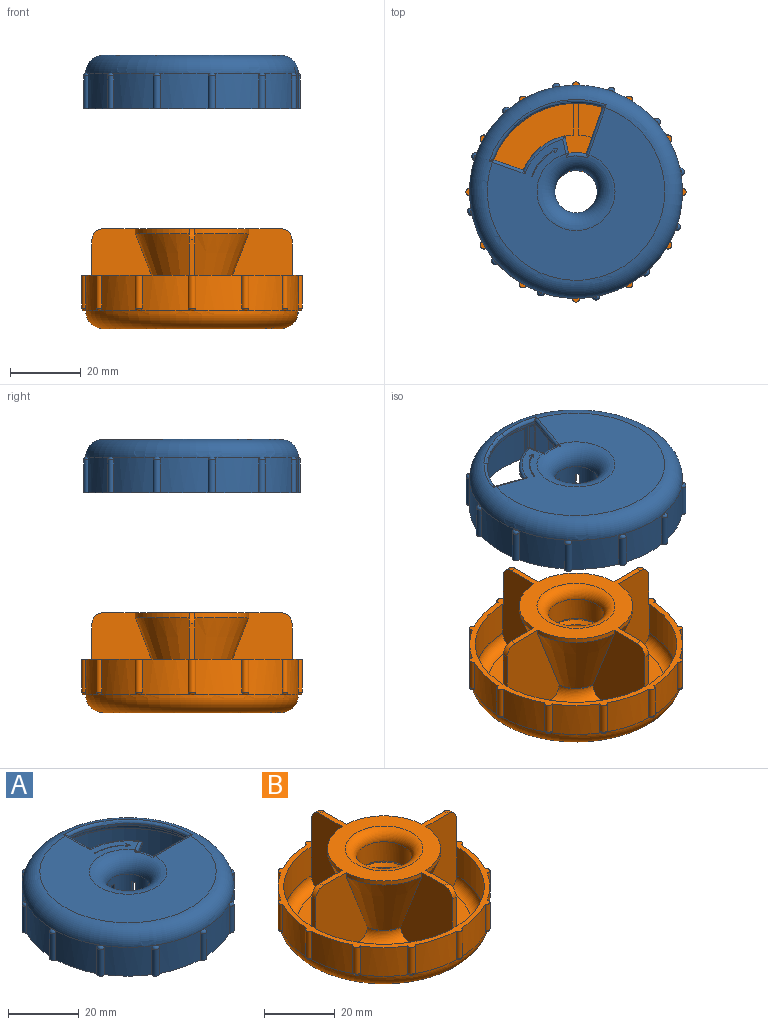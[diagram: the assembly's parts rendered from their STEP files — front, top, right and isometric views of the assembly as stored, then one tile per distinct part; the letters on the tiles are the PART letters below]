
ASSEMBLY  parts=2 mates=1
PART A: 140 faces, bbox 66.1x66.1x16.2 mm
  f0: plane 50x50mm, normal (0,0,1), area 1238.5mm2, adj f77,f103,f117,f119,f120,f123,f127,f128
  f1: cylinder r=7.6mm len=5.77mm, axis (0,0,-1), area 8.6mm2, adj f2,f8,f44,f125
  f2: plane 5.77x4.13mm, normal (0,0,-1), area 9.7mm2, adj f1,f8,f43,f125
  f3: cone r=8.62mm half-angle=41.6deg, axis (0,0,-1), area 6mm2, adj f8,f42,f46,f125
  f4: torus R=7.55mm, axis (0,0,1), area 8.8mm2, adj f5,f7,f11,f16
  f5: cone r=8.62mm half-angle=41.6deg, axis (0,0,1), area 6mm2, adj f4,f7,f9,f16
  f6: plane 1.92x1.73mm, normal (0,0,-1), area 1.7mm2, adj f7,f8,f42,f43
  f7: plane 7.43x2.07mm, normal (0.5,-0.87,0), area 13mm2, adj f4,f5,f6,f9,f10,f11,f42,f43
  f8: plane 7.43x2.07mm, normal (-0.5,0.87,0), area 13mm2, adj f1,f2,f3,f6,f42,f43,f44,f46
  f9: cylinder r=7.6mm len=6.66mm, axis (0,0,-1), area 8.6mm2, adj f5,f7,f10,f16
  f10: plane 6.66x2.16mm, normal (0,0,-1), area 9.7mm2, adj f7,f9,f16,f43
  f11: cone r=8.62mm half-angle=41.6deg, axis (0,0,-1), area 6mm2, adj f4,f7,f16,f42
  f12: torus R=7.55mm, axis (0,0,1), area 8.8mm2, adj f13,f15,f19,f24
  f13: cone r=8.62mm half-angle=41.6deg, axis (0,0,1), area 6mm2, adj f12,f15,f17,f24
  f14: plane 1.92x1.73mm, normal (0,0,-1), area 1.7mm2, adj f15,f16,f42,f43
  f15: plane 7.43x2.07mm, normal (-0.5,-0.87,0), area 13mm2, adj f12,f13,f14,f17,f18,f19,f42,f43
  f16: plane 7.43x2.07mm, normal (0.5,0.87,0), area 13mm2, adj f4,f5,f9,f10,f11,f14,f42,f43
  f17: cylinder r=7.6mm len=5.77mm, axis (0,0,-1), area 8.6mm2, adj f13,f15,f18,f24
  f18: plane 5.77x4.13mm, normal (0,0,-1), area 9.7mm2, adj f15,f17,f24,f43
  f19: cone r=8.62mm half-angle=41.6deg, axis (0,0,-1), area 6mm2, adj f12,f15,f24,f42
  f20: torus R=7.55mm, axis (0,0,1), area 8.8mm2, adj f21,f23,f27,f32
  f21: cone r=8.62mm half-angle=41.6deg, axis (0,0,1), area 6mm2, adj f20,f23,f25,f32
  f22: plane 1.62x1.07mm, normal (0,0,-1), area 1.7mm2, adj f23,f24,f42,f43
  f23: plane 7.43x2.39mm, normal (-1,0,0), area 13mm2, adj f20,f21,f22,f25,f26,f27,f42,f43
  f24: plane 7.43x2.39mm, normal (1,0,0), area 13mm2, adj f12,f13,f17,f18,f19,f22,f42,f43
  f25: cylinder r=7.6mm len=5.77mm, axis (0,0,-1), area 8.6mm2, adj f21,f23,f26,f32
  f26: plane 5.77x4.13mm, normal (0,0,-1), area 9.7mm2, adj f23,f25,f32,f43
  f27: cone r=8.62mm half-angle=41.6deg, axis (0,0,-1), area 6mm2, adj f20,f23,f32,f42
  f28: torus R=7.55mm, axis (0,0,1), area 8.8mm2, adj f29,f31,f35,f40
  f29: cone r=8.62mm half-angle=41.6deg, axis (0,0,1), area 6mm2, adj f28,f31,f33,f40
  f30: plane 1.92x1.73mm, normal (0,0,-1), area 1.7mm2, adj f31,f32,f42,f43
  f31: plane 7.43x2.07mm, normal (-0.5,0.87,0), area 13mm2, adj f28,f29,f30,f33,f34,f35,f42,f43
  f32: plane 7.43x2.07mm, normal (0.5,-0.87,0), area 13mm2, adj f20,f21,f25,f26,f27,f30,f42,f43
  f33: cylinder r=7.6mm len=6.66mm, axis (0,0,-1), area 8.6mm2, adj f29,f31,f34,f40
  f34: plane 6.66x2.16mm, normal (0,0,-1), area 9.7mm2, adj f31,f33,f40,f43
  f35: cone r=8.62mm half-angle=41.6deg, axis (0,0,-1), area 6mm2, adj f28,f31,f40,f42
  f36: torus R=7.55mm, axis (0,0,1), area 8.8mm2, adj f37,f39,f45,f126
  f37: cone r=8.62mm half-angle=41.6deg, axis (0,0,1), area 6mm2, adj f36,f39,f41,f126
  f38: plane 1.92x1.73mm, normal (0,0,-1), area 1.7mm2, adj f39,f40,f42,f43
  f39: plane 7.43x2.07mm, normal (0.5,0.87,0), area 13mm2, adj f36,f37,f38,f41,f42,f43,f45,f53
  f40: plane 7.43x2.07mm, normal (-0.5,-0.87,0), area 13mm2, adj f28,f29,f33,f34,f35,f38,f42,f43
  f41: cylinder r=7.6mm len=5.77mm, axis (0,0,-1), area 8.6mm2, adj f37,f39,f53,f126
  f42: cylinder r=7.6mm len=15.2mm, axis (0,0,-1), area 283.2mm2, adj f3,f6,f7,f8,f11,f14,f15,f16
  f43: cylinder r=6mm len=12mm, axis (0,0,-1), area 329.6mm2, adj f2,f6,f7,f8,f10,f14,f15,f16
  f44: cone r=8.62mm half-angle=41.6deg, axis (0,0,1), area 6mm2, adj f1,f8,f46,f125
  f45: cone r=8.62mm half-angle=41.6deg, axis (0,0,-1), area 6mm2, adj f36,f39,f42,f126
  f46: torus R=7.55mm, axis (0,0,1), area 8.8mm2, adj f3,f8,f44,f125
  f47: cylinder r=28.4mm len=10mm, axis (0,0,-1), area 16.5mm2, adj f51,f52,f104,f106
  f48: cylinder r=28.4mm len=56.8mm, axis (0,0,-1), area 1711mm2, adj f51,f52,f105,f107
  f49: plane 50x50mm, normal (0,0,-1), area 1276.1mm2, adj f50,f51,f109,f110,f111,f112
  f50: torus R=11mm, axis (0,0,1), area 296.5mm2, adj f42,f49,f113
  f51: torus R=25mm, axis (0,0,1), area 906.8mm2, adj f47,f48,f49,f104,f105,f106,f107,f108
  f52: plane 62.13x62.13mm, normal (0,0,-1), area 316.5mm2, adj f47,f48,f79,f80,f81,f82,f83,f84
  f53: plane 5.77x4.13mm, normal (0,0,-1), area 9.7mm2, adj f39,f41,f43,f126
  f54: plane 1.56x1.47mm, normal (0,0,1), area 0.1mm2, adj f76,f77
  f55: plane 1.56x1.47mm, normal (0,0,1), area 0.1mm2, adj f66,f77
  f56: plane 1.6x1.33mm, normal (0,0,1), area 0.1mm2, adj f67,f77
  f57: plane 1.56x1.47mm, normal (0,0,1), area 0.1mm2, adj f68,f77
  f58: plane 1.56x1.47mm, normal (0,0,1), area 0.1mm2, adj f69,f77
  f59: plane 1.6x1.33mm, normal (0,0,1), area 0.1mm2, adj f70,f77
  f60: plane 1.56x1.47mm, normal (0,0,1), area 0.1mm2, adj f71,f77
  f61: plane 1.56x1.47mm, normal (0,0,1), area 0.1mm2, adj f72,f77
  f62: plane 1.6x1.33mm, normal (0,0,1), area 0.1mm2, adj f73,f77
  f63: plane 1.56x1.47mm, normal (0,0,1), area 0.1mm2, adj f74,f77
  f64: plane 1.56x1.47mm, normal (0,0,1), area 0.1mm2, adj f75,f77
  f65: plane 1.6x1.33mm, normal (0,0,1), area 0.1mm2, adj f77,f78
  f66: torus R=0.27mm, axis (0,0,1), area 4.3mm2, adj f55,f79,f100,f102
  f67: torus R=0.27mm, axis (0,0,1), area 4.3mm2, adj f56,f80,f99,f100
  f68: torus R=0.27mm, axis (0,0,1), area 4.3mm2, adj f57,f81,f98,f99
  f69: torus R=0.27mm, axis (0,0,1), area 4.3mm2, adj f58,f82,f97,f98
  f70: torus R=0.27mm, axis (0,0,1), area 4.3mm2, adj f59,f83,f96,f97
  f71: torus R=0.27mm, axis (0,0,1), area 4.3mm2, adj f60,f84,f95,f96
  f72: torus R=0.27mm, axis (0,0,1), area 4.3mm2, adj f61,f85,f94,f95
  f73: torus R=0.27mm, axis (0,0,1), area 4.3mm2, adj f62,f86,f93,f94
  f74: torus R=0.27mm, axis (0,0,1), area 4.3mm2, adj f63,f87,f92,f93
  f75: torus R=0.27mm, axis (0,0,1), area 4.3mm2, adj f64,f88,f91,f92
  f76: torus R=0.27mm, axis (0,0,1), area 4.3mm2, adj f54,f90,f101,f102
  f77: torus R=25mm, axis (0,0,1), area 1352.4mm2, adj f0,f54,f55,f56,f57,f58,f59,f60
  f78: torus R=0.27mm, axis (0,0,1), area 4.3mm2, adj f65,f89,f90,f91
  f79: cylinder r=1.07mm len=9.2mm, axis (0,0,-1), area 31.2mm2, adj f52,f66,f100,f102
  f80: cylinder r=1.07mm len=9.2mm, axis (0,0,-1), area 31.2mm2, adj f52,f67,f99,f100
  f81: cylinder r=1.07mm len=9.2mm, axis (0,0,-1), area 31.2mm2, adj f52,f68,f98,f99
  f82: cylinder r=1.07mm len=9.2mm, axis (0,0,-1), area 31.2mm2, adj f52,f69,f97,f98
  f83: cylinder r=1.07mm len=9.2mm, axis (0,0,-1), area 31.2mm2, adj f52,f70,f96,f97
  f84: cylinder r=1.07mm len=9.2mm, axis (0,0,-1), area 31.2mm2, adj f52,f71,f95,f96
  f85: cylinder r=1.07mm len=9.2mm, axis (0,0,-1), area 31.2mm2, adj f52,f72,f94,f95
  f86: cylinder r=1.07mm len=9.2mm, axis (0,0,-1), area 31.2mm2, adj f52,f73,f93,f94
  f87: cylinder r=1.07mm len=9.2mm, axis (0,0,-1), area 31.2mm2, adj f52,f74,f92,f93
  f88: cylinder r=1.07mm len=9.2mm, axis (0,0,-1), area 31.2mm2, adj f52,f75,f91,f92
  f89: cylinder r=1.07mm len=9.2mm, axis (0,0,-1), area 31.2mm2, adj f52,f78,f90,f91
  f90: cylinder r=30mm len=14.5mm, axis (0,0,-1), area 136.4mm2, adj f52,f76,f77,f78,f89,f101
  f91: cylinder r=30mm len=14.5mm, axis (0,0,-1), area 136.4mm2, adj f52,f75,f77,f78,f88,f89
  f92: cylinder r=30mm len=10.62mm, axis (0,0,-1), area 136.4mm2, adj f52,f74,f75,f77,f87,f88
  f93: cylinder r=30mm len=14.5mm, axis (0,0,-1), area 136.4mm2, adj f52,f73,f74,f77,f86,f87
  f94: cylinder r=30mm len=14.5mm, axis (0,0,-1), area 136.4mm2, adj f52,f72,f73,f77,f85,f86
  f95: cylinder r=30mm len=10.62mm, axis (0,0,-1), area 136.4mm2, adj f52,f71,f72,f77,f84,f85
  f96: cylinder r=30mm len=14.5mm, axis (0,0,-1), area 136.4mm2, adj f52,f70,f71,f77,f83,f84
  f97: cylinder r=30mm len=14.5mm, axis (0,0,-1), area 136.4mm2, adj f52,f69,f70,f77,f82,f83
  f98: cylinder r=30mm len=10.62mm, axis (0,0,-1), area 136.4mm2, adj f52,f68,f69,f77,f81,f82
  f99: cylinder r=30mm len=14.5mm, axis (0,0,-1), area 136.4mm2, adj f52,f67,f68,f77,f80,f81
  f100: cylinder r=30mm len=14.5mm, axis (0,0,-1), area 136.4mm2, adj f52,f66,f67,f77,f79,f80
  f101: cylinder r=1.07mm len=9.2mm, axis (0,0,-1), area 31.2mm2, adj f52,f76,f90,f102
  f102: cylinder r=30mm len=10.62mm, axis (0,0,-1), area 136.4mm2, adj f52,f66,f76,f77,f79,f101
  f103: torus R=11mm, axis (0,0,1), area 379.6mm2, adj f0,f43,f114,f115,f116
  f104: plane 11.61x0.41mm, normal (0,1,0), area 4.4mm2, adj f47,f51,f52,f105
  f105: plane 12.75x5.17mm, normal (-1,0,0), area 45mm2, adj f48,f51,f52,f104
  f106: plane 11.98x1.18mm, normal (-0.88,-0.48,0), area 10.1mm2, adj f47,f51,f52,f107
  f107: plane 11.98x1.22mm, normal (-0.93,0.37,0), area 10.1mm2, adj f48,f51,f52,f106
  f108: cylinder r=25mm len=24.19mm, axis (0,0,-1), area 27.2mm2, adj f51,f109,f111,f122
  f109: plane 9.01x0.8mm, normal (1,0,0), area 7.2mm2, adj f49,f108,f110,f122,f123
  f110: cylinder r=16mm len=12.99mm, axis (0,0,-1), area 12.7mm2, adj f49,f109,f112,f120
  f111: plane 14.02x0.8mm, normal (0,1,0), area 11.2mm2, adj f49,f108,f113,f114,f116,f119,f122
  f112: plane 4.31x2.54mm, normal (0.51,-0.86,0), area 4mm2, adj f49,f110,f113,f114,f117
  f113: cylinder r=11mm len=4.77mm, axis (0,0,-1), area 3.6mm2, adj f50,f111,f112,f114
  f114: torus R=10.2mm, axis (0,0,1), area 7.6mm2, adj f103,f111,f112,f113,f115,f116,f117
  f115: bspline ~2.79x2.11mm, area 0.5mm2, adj f103,f114,f117
  f116: torus R=4.2mm, axis (0,-1,0), area 0.5mm2, adj f103,f111,f114,f119
  f117: cylinder r=0.8mm len=4.74mm, axis (0.86,0.51,0), area 5.9mm2, adj f0,f112,f114,f115,f120
  f118: torus R=4.2mm, axis (0,-1,0), area 0.6mm2, adj f77,f119,f122
  f119: cylinder r=0.8mm len=14mm, axis (-1,0,0), area 17.6mm2, adj f0,f111,f116,f118,f122
  f120: torus R=15.2mm, axis (0,0,1), area 19.5mm2, adj f0,f110,f117,f123
  f121: torus R=4.2mm, axis (1,0,0), area 0.6mm2, adj f77,f122,f123
  f122: torus R=25.8mm, axis (0,0,-1), area 54.7mm2, adj f77,f108,f109,f111,f118,f119,f121,f123
  f123: cylinder r=0.8mm len=9.8mm, axis (0,1,0), area 11.7mm2, adj f0,f109,f120,f121,f122
  f124: plane 1.62x1.07mm, normal (0,0,-1), area 1.7mm2, adj f42,f43,f125,f126
  f125: plane 7.43x2.39mm, normal (1,0,0), area 13mm2, adj f1,f2,f3,f42,f43,f44,f46,f124
  f126: plane 7.43x2.39mm, normal (-1,0,0), area 13mm2, adj f36,f37,f41,f42,f43,f45,f53,f124
  f127: cylinder r=13mm len=8.83mm, axis (0,0,1), area 2.9mm2, adj f0,f128,f138,f139
  f128: plane 0.3x0.24mm, normal (0.68,-0.73,0), area 0.1mm2, adj f0,f127,f129,f139
  f129: plane 0.3x0.06mm, normal (-0.3,-0.96,0), area 0mm2, adj f0,f128,f130,f139
  f130: cylinder r=0.1mm len=0.3mm, axis (0,0,1), area 0.1mm2, adj f0,f129,f131,f139
  f131: plane 1.1x0.34mm, normal (0.3,0.96,0), area 0.3mm2, adj f0,f130,f132,f139
  f132: cylinder r=0.1mm len=0.3mm, axis (0,0,1), area 0.1mm2, adj f0,f131,f133,f139
  f133: plane 1.13x0.3mm, normal (-0.98,-0.22,0), area 0.3mm2, adj f0,f132,f134,f139
  f134: cylinder r=0.1mm len=0.3mm, axis (0,0,1), area 0.1mm2, adj f0,f133,f135,f139
  f135: plane 0.3x0.06mm, normal (0.98,0.22,0), area 0mm2, adj f0,f134,f136,f139
  f136: plane 0.3x0.29mm, normal (0.68,-0.73,0), area 0.1mm2, adj f0,f135,f137,f139
  f137: cylinder r=13.2mm len=8.98mm, axis (0,0,1), area 3mm2, adj f0,f136,f138,f139
  f138: cylinder r=0.1mm len=0.3mm, axis (0,0,1), area 0.1mm2, adj f0,f127,f137,f139
  f139: plane 9.81x4.4mm, normal (0,0,1), area 2.8mm2, adj f127,f128,f129,f130,f131,f132,f133,f134
PART B: 104 faces, bbox 65.2x65.2x28.4 mm
  f0: cylinder r=16mm len=15.18mm, axis (0,0,-1), area 32.9mm2, adj f4,f12,f17,f92
  f1: cylinder r=16mm len=15.18mm, axis (0,0,-1), area 32.9mm2, adj f10,f11,f23,f92
  f2: cylinder r=16mm len=15.18mm, axis (0,0,-1), area 32.9mm2, adj f8,f9,f30,f92
  f3: cylinder r=6mm len=12mm, axis (0,0,-1), area 369.5mm2, adj f79,f101
  f4: plane 26.84x21.07mm, normal (0,-1,0), area 441.1mm2, adj f0,f13,f14,f15,f16,f17,f83,f85
  f5: plane 26.84x21.07mm, normal (0,1,0), area 441.1mm2, adj f6,f28,f31,f83,f84,f86,f87,f88
  f6: cylinder r=16mm len=15.18mm, axis (0,0,-1), area 32.9mm2, adj f5,f7,f88,f92
  f7: plane 26.84x21.07mm, normal (1,0,0), area 441.1mm2, adj f6,f28,f31,f83,f84,f86,f87,f88
  f8: plane 26.84x21.07mm, normal (-1,0,0), area 441.1mm2, adj f2,f24,f25,f26,f27,f29,f30,f83
  f9: plane 26.84x21.07mm, normal (0,1,0), area 441.1mm2, adj f2,f24,f25,f26,f27,f29,f30,f83
  f10: plane 26.84x21.07mm, normal (0,-1,0), area 441.1mm2, adj f1,f18,f19,f20,f21,f22,f23,f83
  f11: plane 26.84x21.07mm, normal (-1,0,0), area 441.1mm2, adj f1,f18,f19,f20,f21,f22,f23,f83
  f12: plane 26.84x21.07mm, normal (1,0,0), area 441.1mm2, adj f0,f13,f14,f15,f16,f17,f83,f85
  f13: cylinder r=7.6mm len=6.76mm, axis (0,0,-1), area 1.1mm2, adj f4,f12,f15,f17
  f14: cylinder r=28.4mm len=27.59mm, axis (0,0,-1), area 430.1mm2, adj f4,f12,f16,f83
  f15: torus R=11mm, axis (0,0,1), area 65.8mm2, adj f4,f12,f13,f85
  f16: torus R=25mm, axis (0,0,1), area 219.2mm2, adj f4,f12,f14,f85
  f17: cone r=7.56mm half-angle=21.2deg, axis (0,0,1), area 390.3mm2, adj f0,f4,f12,f13
  f18: plane 24.19x24.19mm, normal (0,0,1), area 373.4mm2, adj f10,f11,f21,f22
  f19: cylinder r=7.6mm len=6.76mm, axis (0,0,-1), area 1.1mm2, adj f10,f11,f21,f23
  f20: cylinder r=28.4mm len=27.59mm, axis (0,0,-1), area 430.1mm2, adj f10,f11,f22,f83
  f21: torus R=11mm, axis (0,0,1), area 65.8mm2, adj f10,f11,f18,f19
  f22: torus R=25mm, axis (0,0,1), area 219.2mm2, adj f10,f11,f18,f20
  f23: cone r=7.56mm half-angle=21.2deg, axis (0,0,1), area 390.3mm2, adj f1,f10,f11,f19
  f24: plane 24.19x24.19mm, normal (0,0,1), area 373.4mm2, adj f8,f9,f27,f29
  f25: cylinder r=7.6mm len=6.76mm, axis (0,0,-1), area 1.1mm2, adj f8,f9,f27,f30
  f26: cylinder r=28.4mm len=27.59mm, axis (0,0,-1), area 430.1mm2, adj f8,f9,f29,f83
  f27: torus R=11mm, axis (0,0,1), area 65.8mm2, adj f8,f9,f24,f25
  f28: plane 24.19x24.19mm, normal (0,0,1), area 373.4mm2, adj f5,f7,f84,f86
  f29: torus R=25mm, axis (0,0,1), area 219.2mm2, adj f8,f9,f24,f26
  f30: cone r=7.56mm half-angle=21.2deg, axis (0,0,1), area 390.3mm2, adj f2,f8,f9,f25
  f31: cylinder r=7.6mm len=6.76mm, axis (0,0,-1), area 1.1mm2, adj f5,f7,f84,f88
  f32: cylinder r=30mm len=10.62mm, axis (0,0,-1), area 136mm2, adj f33,f35,f56,f58,f80,f83
  f33: cylinder r=1.07mm len=9.2mm, axis (0,0,-1), area 31.2mm2, adj f32,f54,f56,f83
  f34: cylinder r=30mm len=14.5mm, axis (0,0,-1), area 136mm2, adj f35,f37,f58,f60,f80,f83
  f35: cylinder r=1.07mm len=9.2mm, axis (0,0,-1), area 31.2mm2, adj f32,f34,f58,f83
  f36: cylinder r=30mm len=14.5mm, axis (0,0,-1), area 136mm2, adj f37,f39,f60,f62,f80,f83
  f37: cylinder r=1.07mm len=9.2mm, axis (0,0,-1), area 31.2mm2, adj f34,f36,f60,f83
  f38: cylinder r=30mm len=10.62mm, axis (0,0,-1), area 136mm2, adj f39,f41,f62,f64,f80,f83
  f39: cylinder r=1.07mm len=9.2mm, axis (0,0,-1), area 31.2mm2, adj f36,f38,f62,f83
  f40: cylinder r=30mm len=14.5mm, axis (0,0,-1), area 136mm2, adj f41,f43,f64,f66,f80,f83
  f41: cylinder r=1.07mm len=9.2mm, axis (0,0,-1), area 31.2mm2, adj f38,f40,f64,f83
  f42: cylinder r=30mm len=14.5mm, axis (0,0,-1), area 136mm2, adj f43,f45,f66,f68,f80,f83
  f43: cylinder r=1.07mm len=9.2mm, axis (0,0,-1), area 31.2mm2, adj f40,f42,f66,f83
  f44: cylinder r=30mm len=10.62mm, axis (0,0,-1), area 136mm2, adj f45,f47,f68,f70,f80,f83
  f45: cylinder r=1.07mm len=9.2mm, axis (0,0,-1), area 31.2mm2, adj f42,f44,f68,f83
  f46: cylinder r=30mm len=14.5mm, axis (0,0,-1), area 136mm2, adj f47,f49,f70,f72,f80,f83
  f47: cylinder r=1.07mm len=9.2mm, axis (0,0,-1), area 31.2mm2, adj f44,f46,f70,f83
  f48: cylinder r=30mm len=14.5mm, axis (0,0,-1), area 136mm2, adj f49,f51,f72,f74,f80,f83
  f49: cylinder r=1.07mm len=9.2mm, axis (0,0,-1), area 31.2mm2, adj f46,f48,f72,f83
  f50: cylinder r=30mm len=10.62mm, axis (0,0,-1), area 136mm2, adj f51,f53,f74,f76,f80,f83
  f51: cylinder r=1.07mm len=9.2mm, axis (0,0,-1), area 31.2mm2, adj f48,f50,f74,f83
  f52: cylinder r=30mm len=14.5mm, axis (0,0,-1), area 136mm2, adj f53,f55,f76,f80,f82,f83
  f53: cylinder r=1.07mm len=9.2mm, axis (0,0,-1), area 31.2mm2, adj f50,f52,f76,f83
  f54: cylinder r=30mm len=14.5mm, axis (0,0,-1), area 136mm2, adj f33,f55,f56,f80,f82,f83
  f55: cylinder r=1.07mm len=9.2mm, axis (0,0,-1), area 31.2mm2, adj f52,f54,f82,f83
  f56: torus R=0.27mm, axis (0,0,1), area 3.1mm2, adj f32,f33,f54,f57
  f57: plane 0.5x0.4mm, normal (0,0,-1), area 0.1mm2, adj f56,f80
  f58: torus R=0.27mm, axis (0,0,1), area 3.1mm2, adj f32,f34,f35,f59
  f59: plane 0.5x0.4mm, normal (0,0,-1), area 0.1mm2, adj f58,f80
  f60: torus R=0.27mm, axis (0,0,1), area 3.1mm2, adj f34,f36,f37,f61
  f61: plane 0.53x0.27mm, normal (0,0,-1), area 0.1mm2, adj f60,f80
  f62: torus R=0.27mm, axis (0,0,1), area 3.1mm2, adj f36,f38,f39,f63
  f63: plane 0.5x0.4mm, normal (0,0,-1), area 0.1mm2, adj f62,f80
  f64: torus R=0.27mm, axis (0,0,1), area 3.1mm2, adj f38,f40,f41,f65
  f65: plane 0.5x0.4mm, normal (0,0,-1), area 0.1mm2, adj f64,f80
  f66: torus R=0.27mm, axis (0,0,1), area 3.1mm2, adj f40,f42,f43,f67
  f67: plane 0.53x0.27mm, normal (0,0,-1), area 0.1mm2, adj f66,f80
  f68: torus R=0.27mm, axis (0,0,1), area 3.1mm2, adj f42,f44,f45,f69
  f69: plane 0.5x0.4mm, normal (0,0,-1), area 0.1mm2, adj f68,f80
  f70: torus R=0.27mm, axis (0,0,1), area 3.1mm2, adj f44,f46,f47,f71
  f71: plane 0.5x0.4mm, normal (0,0,-1), area 0.1mm2, adj f70,f80
  f72: torus R=0.27mm, axis (0,0,1), area 3.1mm2, adj f46,f48,f49,f73
  f73: plane 0.53x0.27mm, normal (0,0,-1), area 0.1mm2, adj f72,f80
  f74: torus R=0.27mm, axis (0,0,1), area 3.1mm2, adj f48,f50,f51,f75
  f75: plane 0.5x0.4mm, normal (0,0,-1), area 0.1mm2, adj f74,f80
  f76: torus R=0.27mm, axis (0,0,1), area 3.1mm2, adj f50,f52,f53,f77
  f77: plane 0.5x0.4mm, normal (0,0,-1), area 0.1mm2, adj f76,f80
  f78: plane 50x50mm, normal (0,0,-1), area 1583.4mm2, adj f79,f80
  f79: torus R=11mm, axis (0,0,1), area 385.7mm2, adj f3,f78
  f80: torus R=25mm, axis (0,0,1), area 1390.8mm2, adj f32,f34,f36,f38,f40,f42,f44,f46
  f81: plane 0.53x0.27mm, normal (0,0,-1), area 0.1mm2, adj f80,f82
  f82: torus R=0.27mm, axis (0,0,1), area 3.1mm2, adj f52,f54,f55,f81
  f83: plane 62.13x62.13mm, normal (0,0,1), area 316.4mm2, adj f4,f5,f7,f8,f9,f10,f11,f12
  f84: torus R=11mm, axis (0,0,1), area 65.8mm2, adj f5,f7,f28,f31
  f85: plane 24.19x24.19mm, normal (0,0,1), area 373.4mm2, adj f4,f12,f15,f16
  f86: torus R=25mm, axis (0,0,1), area 219.2mm2, adj f5,f7,f28,f87
  f87: cylinder r=28.4mm len=27.59mm, axis (0,0,-1), area 430.1mm2, adj f5,f7,f83,f86
  f88: cone r=7.56mm half-angle=21.2deg, axis (0,0,1), area 390.3mm2, adj f5,f6,f7,f31
  f89: cylinder r=28.2mm len=10mm, axis (0,0,-1), area 16mm2, adj f4,f5,f83,f93
  f90: cylinder r=28.2mm len=10mm, axis (0,0,-1), area 16mm2, adj f7,f8,f83,f94
  f91: cylinder r=28.2mm len=10mm, axis (0,0,-1), area 16mm2, adj f9,f10,f83,f95
  f92: plane 50x50mm, normal (0,0,1), area 481.7mm2, adj f0,f1,f2,f4,f5,f6,f7,f8
  f93: torus R=25mm, axis (0,0,1), area 8.2mm2, adj f4,f5,f89,f92
  f94: torus R=25mm, axis (0,0,1), area 8.2mm2, adj f7,f8,f90,f92
  f95: torus R=25mm, axis (0,0,1), area 8.2mm2, adj f9,f10,f91,f92
  f96: cylinder r=7.8mm len=15.6mm, axis (0,0,-1), area 67.2mm2, adj f101,f102
  f97: cylinder r=7.8mm len=15.6mm, axis (0,0,-1), area 327mm2, adj f99,f103
  f98: cylinder r=28.2mm len=10mm, axis (0,0,-1), area 16mm2, adj f11,f12,f83,f100
  f99: torus R=11mm, axis (0,0,1), area 283.1mm2, adj f92,f97
  f100: torus R=25mm, axis (0,0,1), area 8.2mm2, adj f11,f12,f92,f98
  f101: plane 15.6x15.6mm, normal (0,0,1), area 78mm2, adj f3,f96
  f102: cone r=8.77mm half-angle=41.6deg, axis (0,0,1), area 75mm2, adj f96,f103
  f103: cone r=8.62mm half-angle=41.6deg, axis (0,0,-1), area 75mm2, adj f97,f102
PLACE A rot(axis=(0,0,1),70.8deg) t=(0,0,47.03)mm
PLACE B at identity fixed
MATE cylindrical B.f14 <-> A.f1  axis (0,0,1) through (0,0,0)mm
